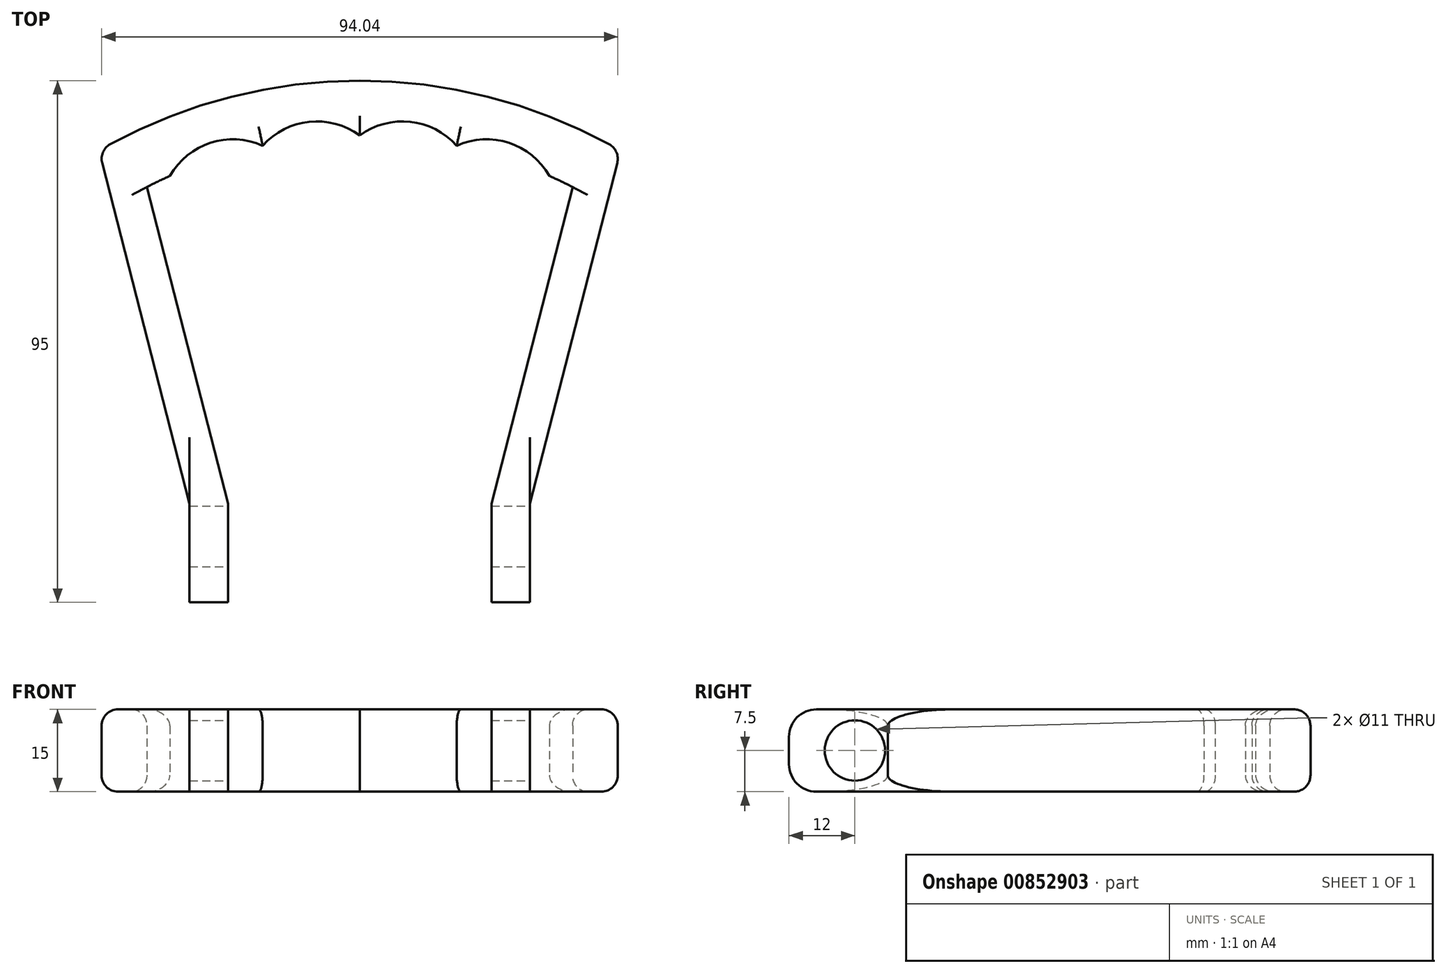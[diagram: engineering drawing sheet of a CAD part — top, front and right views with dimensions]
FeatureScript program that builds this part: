
annotation { "Feature Type Name" : "Feature", "Feature Type Description" : "" }
export const myFeature = defineFeature(function(context is Context, id is Id, definition is map)
    precondition{}
    {
        {
            var Q0;
            Q0=qCreatedBy(makeId("Top.planeOp"),FACE);
            var sketch = newSketch(context, id + "F0", { "sketchPlane" : qUnion([Q0])});
            skLineSegment(sketch, "E0.bottom", {"start": v(24, 18) * mm, "end": v(31, 18) * mm});
            skLineSegment(sketch, "E0.top", {"start": v(24, 0) * mm, "end": v(31, 0) * mm});
            skLineSegment(sketch, "E0.left", {"start": v(24, 18) * mm, "end": v(24, 0) * mm});
            skLineSegment(sketch, "E0.right", {"start": v(31, 18) * mm, "end": v(31, 0) * mm});
            skLineSegment(sketch, "E1.bottom", {"start": v(-31, 18) * mm, "end": v(-24, 18) * mm});
            skLineSegment(sketch, "E1.top", {"start": v(-31, 0) * mm, "end": v(-24, 0) * mm});
            skLineSegment(sketch, "E1.left", {"start": v(-31, 18) * mm, "end": v(-31, 0) * mm});
            skLineSegment(sketch, "E1.right", {"start": v(-24, 18) * mm, "end": v(-24, 0) * mm});
            skArc(sketch, "E2", {"start": v(-47.5, 82.27) * mm, "mid": v(0, 95) * mm, "end": v(47.5, 82.27) * mm});
            skArc(sketch, "E3", {"start": v(-42.5, 73.61) * mm, "mid": v(0, 85) * mm, "end": v(42.5, 73.61) * mm});
            skLineSegment(sketch, "E4", {"start": v(-47.5, 82.27) * mm, "end": v(0, 0) * mm, "construction": true});
            skLineSegment(sketch, "E5", {"start": v(47.5, 82.27) * mm, "end": v(0, 0) * mm, "construction": true});
            skLineSegment(sketch, "E6", {"start": v(-31, 18) * mm, "end": v(-47.5, 82.27) * mm});
            skLineSegment(sketch, "E7", {"start": v(-24, 18) * mm, "end": v(-38.8, 75.63) * mm});
            skLineSegment(sketch, "E8", {"start": v(31, 18) * mm, "end": v(47.5, 82.27) * mm});
            skLineSegment(sketch, "E9", {"start": v(24, 18) * mm, "end": v(38.8, 75.63) * mm});
            skArc(sketch, "E10", {"start": v(-44, 76.21) * mm, "mid": v(0, 88) * mm, "end": v(44, 76.21) * mm, "construction": true});
            skLineSegment(sketch, "E11", {"start": v(0, 0) * mm, "end": v(-27.2, 83.7) * mm, "construction": true});
            skLineSegment(sketch, "E12", {"start": v(0, 0) * mm, "end": v(-9.2, 87.52) * mm, "construction": true});
            skLineSegment(sketch, "E13", {"start": v(9.2, 87.52) * mm, "end": v(0, 0) * mm, "construction": true});
            skLineSegment(sketch, "E14", {"start": v(27.2, 83.7) * mm, "end": v(0, 0) * mm, "construction": true});
            skArc(sketch, "E15", {"start": v(-17.67, 83.14) * mm, "mid": v(-27.2, 83.7) * mm, "end": v(-34.57, 77.65) * mm});
            skArc(sketch, "E16", {"start": v(0, 85) * mm, "mid": v(-9.2, 87.52) * mm, "end": v(-17.67, 83.14) * mm});
            skArc(sketch, "E17", {"start": v(17.67, 83.14) * mm, "mid": v(9.2, 87.52) * mm, "end": v(0, 85) * mm});
            skArc(sketch, "E18", {"start": v(34.57, 77.65) * mm, "mid": v(27.2, 83.7) * mm, "end": v(17.67, 83.14) * mm});
            skLineSegment(sketch, "E19", {"start": v(-17.67, 83.14) * mm, "end": v(0, 0) * mm, "construction": true});
            skLineSegment(sketch, "E20", {"start": v(17.67, 83.14) * mm, "end": v(0, 0) * mm, "construction": true});
            skSolve(sketch);
        }
        {
            var Q0;
            Q0=makeQuery(id+"F0.imprint","IMPRINT",FACE,{"disambiguationData":[TD([[makeQuery(id+"F0.imprint","IMPRINT",EDGE,{"derivedFrom":sQuery(id+"F0.wireOp",EDGE,"E0.bottom")}),1.0]])]});
            var Q1;
            Q1=makeQuery(id+"F0.imprint","IMPRINT",FACE,{"disambiguationData":[TD([[makeQuery(id+"F0.imprint","IMPRINT",EDGE,{"derivedFrom":sQuery(id+"F0.wireOp",EDGE,"E1.bottom")}),-1.0]])]});
            var Q2;
            Q2=makeQuery(id+"F0.imprint","IMPRINT",FACE,{"disambiguationData":[TD([[makeQuery(id+"F0.imprint","IMPRINT",EDGE,{"derivedFrom":sQuery(id+"F0.wireOp",EDGE,"E0.bottom")}),-1.0]])]});
            extrude(context, id + "F1", {"entities" : qUnion([Q0, Q1, Q2]), "depth" : 15 * mm, "offsetDistance" : 25 * mm});
        }
        {
            var Q0;
            Q0=makeQuery(id+"F1.opExtrude","CAP_EDGE",EDGE,{"disambiguationData":[OSD([sQuery(id+"F0.wireOp",EDGE,"E9")])],"isStart":false});
            var Q1;
            {var subQ0=sQuery(id+"F0.wireOp",EDGE,"E3");Q1=makeQuery(id+"F1.opExtrude","CAP_EDGE",EDGE,{"disambiguationData":[OSD([subQ0]),TDD([makeQuery(id+"F0.imprint","IMPRINT",EDGE,{"disambiguationData":[TD([[makeQuery(id+"F0.imprint","INTERSECT",VERTEX,{"derivedFrom":[subQ0,sQuery(id+"F0.wireOp",EDGE,"E9")]}),1.0]])],"derivedFrom":subQ0})])],"isStart":false});}
            var Q2;
            Q2=makeQuery(id+"F1.opExtrude","CAP_EDGE",EDGE,{"disambiguationData":[OSD([sQuery(id+"F0.wireOp",EDGE,"E18")])],"isStart":false});
            var Q3;
            Q3=makeQuery(id+"F1.opExtrude","CAP_EDGE",EDGE,{"disambiguationData":[OSD([sQuery(id+"F0.wireOp",EDGE,"E17")])],"isStart":false});
            var Q4;
            Q4=makeQuery(id+"F1.opExtrude","CAP_EDGE",EDGE,{"disambiguationData":[OSD([sQuery(id+"F0.wireOp",EDGE,"E16")])],"isStart":false});
            var Q5;
            {var subQ0=sQuery(id+"F0.wireOp",EDGE,"E3");Q5=makeQuery(id+"F1.opExtrude","CAP_EDGE",EDGE,{"disambiguationData":[OSD([subQ0]),TDD([makeQuery(id+"F0.imprint","IMPRINT",EDGE,{"disambiguationData":[TD([[makeQuery(id+"F0.imprint","INTERSECT",VERTEX,{"derivedFrom":[subQ0,sQuery(id+"F0.wireOp",EDGE,"E7")]}),-1.0]])],"derivedFrom":subQ0})])],"isStart":false});}
            var Q6;
            Q6=makeQuery(id+"F1.opExtrude","CAP_EDGE",EDGE,{"disambiguationData":[OSD([sQuery(id+"F0.wireOp",EDGE,"E15")])],"isStart":false});
            var Q7;
            Q7=makeQuery(id+"F1.opExtrude","CAP_EDGE",EDGE,{"disambiguationData":[OSD([sQuery(id+"F0.wireOp",EDGE,"E7")])],"isStart":false});
            var Q8;
            Q8=makeQuery(id+"F1.opExtrude","CAP_EDGE",EDGE,{"disambiguationData":[OSD([sQuery(id+"F0.wireOp",EDGE,"E2")])],"isStart":false});
            var Q9;
            Q9=makeQuery(id+"F1.opExtrude","CAP_EDGE",EDGE,{"disambiguationData":[OSD([sQuery(id+"F0.wireOp",EDGE,"E6")])],"isStart":false});
            var Q10;
            Q10=makeQuery(id+"F1.opExtrude","CAP_EDGE",EDGE,{"disambiguationData":[OSD([sQuery(id+"F0.wireOp",EDGE,"E8")])],"isStart":false});
            var Q11;
            Q11=makeQuery(id+"F1.opExtrude","CAP_EDGE",EDGE,{"disambiguationData":[OSD([sQuery(id+"F0.wireOp",EDGE,"E6")])],"isStart":true});
            var Q12;
            Q12=makeQuery(id+"F1.opExtrude","CAP_EDGE",EDGE,{"disambiguationData":[OSD([sQuery(id+"F0.wireOp",EDGE,"E7")])],"isStart":true});
            var Q13;
            Q13=makeQuery(id+"F1.opExtrude","CAP_EDGE",EDGE,{"disambiguationData":[OSD([sQuery(id+"F0.wireOp",EDGE,"E9")])],"isStart":true});
            var Q14;
            Q14=makeQuery(id+"F1.opExtrude","CAP_EDGE",EDGE,{"disambiguationData":[OSD([sQuery(id+"F0.wireOp",EDGE,"E2")])],"isStart":true});
            var Q15;
            {var subQ0=sQuery(id+"F0.wireOp",EDGE,"E3");Q15=makeQuery(id+"F1.opExtrude","CAP_EDGE",EDGE,{"disambiguationData":[OSD([subQ0]),TDD([makeQuery(id+"F0.imprint","IMPRINT",EDGE,{"disambiguationData":[TD([[makeQuery(id+"F0.imprint","INTERSECT",VERTEX,{"derivedFrom":[subQ0,sQuery(id+"F0.wireOp",EDGE,"E7")]}),-1.0]])],"derivedFrom":subQ0})])],"isStart":true});}
            var Q16;
            {var subQ0=sQuery(id+"F0.wireOp",EDGE,"E3");Q16=makeQuery(id+"F1.opExtrude","CAP_EDGE",EDGE,{"disambiguationData":[OSD([subQ0]),TDD([makeQuery(id+"F0.imprint","IMPRINT",EDGE,{"disambiguationData":[TD([[makeQuery(id+"F0.imprint","INTERSECT",VERTEX,{"derivedFrom":[subQ0,sQuery(id+"F0.wireOp",EDGE,"E9")]}),1.0]])],"derivedFrom":subQ0})])],"isStart":true});}
            var Q17;
            Q17=makeQuery(id+"F1.opExtrude","CAP_EDGE",EDGE,{"disambiguationData":[OSD([sQuery(id+"F0.wireOp",EDGE,"E18")])],"isStart":true});
            var Q18;
            Q18=makeQuery(id+"F1.opExtrude","CAP_EDGE",EDGE,{"disambiguationData":[OSD([sQuery(id+"F0.wireOp",EDGE,"E17")])],"isStart":true});
            var Q19;
            Q19=makeQuery(id+"F1.opExtrude","CAP_EDGE",EDGE,{"disambiguationData":[OSD([sQuery(id+"F0.wireOp",EDGE,"E16")])],"isStart":true});
            var Q20;
            Q20=makeQuery(id+"F1.opExtrude","CAP_EDGE",EDGE,{"disambiguationData":[OSD([sQuery(id+"F0.wireOp",EDGE,"E15")])],"isStart":true});
            var Q21;
            Q21=makeQuery(id+"F1.opExtrude","CAP_EDGE",EDGE,{"disambiguationData":[OSD([sQuery(id+"F0.wireOp",EDGE,"E8")])],"isStart":true});
            var Q22;
            Q22=makeQuery(id+"F1.opExtrude","SWEPT_EDGE",EDGE,{"disambiguationData":[OSD([sQuery(id+"F0.wireOp",EDGE,"E2"),sQuery(id+"F0.wireOp",EDGE,"E6")])]});
            var Q23;
            Q23=makeQuery(id+"F1.opExtrude","SWEPT_EDGE",EDGE,{"disambiguationData":[OSD([sQuery(id+"F0.wireOp",EDGE,"E2"),sQuery(id+"F0.wireOp",EDGE,"E8")])]});
            fillet(context, id + "F2", {"entities" : qUnion([Q0, Q1, Q2, Q3, Q4, Q5, Q6, Q7, Q8, Q9, Q10, Q11, Q12, Q13, Q14, Q15, Q16, Q17, Q18, Q19, Q20, Q21, Q22, Q23]), "radius" : 3 * mm, "tangentPropagation" : true, "allowEdgeOverflow" : false});
        }
        {
            var Q0;
            Q0=makeQuery(id+"F1.opExtrude","CAP_EDGE",EDGE,{"disambiguationData":[OSD([sQuery(id+"F0.wireOp",EDGE,"E0.top")])],"isStart":true});
            var Q1;
            Q1=makeQuery(id+"F1.opExtrude","CAP_EDGE",EDGE,{"disambiguationData":[OSD([sQuery(id+"F0.wireOp",EDGE,"E0.top")])],"isStart":false});
            var Q2;
            Q2=makeQuery(id+"F1.opExtrude","CAP_EDGE",EDGE,{"disambiguationData":[OSD([sQuery(id+"F0.wireOp",EDGE,"E1.top")])],"isStart":true});
            var Q3;
            Q3=makeQuery(id+"F1.opExtrude","CAP_EDGE",EDGE,{"disambiguationData":[OSD([sQuery(id+"F0.wireOp",EDGE,"E1.top")])],"isStart":false});
            fillet(context, id + "F3", {"entities" : qUnion([Q0, Q1, Q2, Q3]), "radius" : 5 * mm, "tangentPropagation" : true, "allowEdgeOverflow" : false});
        }
        {
            var Q0;
            Q0=makeQuery(id+"F1.opExtrude","SWEPT_FACE",FACE,{"disambiguationData":[OSD([sQuery(id+"F0.wireOp",EDGE,"E0.right")])]});
            var sketch = newSketch(context, id + "F4", { "sketchPlane" : qUnion([Q0])});
            skCircle(sketch, "E21", {"center": v(12, 7.5) * mm, "radius": 5.5 * mm});
            skSolve(sketch);
        }
        {
            var Q0;
            Q0=makeQuery(id+"F4.imprint","IMPRINT",FACE,{"disambiguationData":[TD([[makeQuery(id+"F4.imprint","IMPRINT",EDGE,{"derivedFrom":sQuery(id+"F4.wireOp",EDGE,"E21")}),1.0]])]});
            extrude(context, id + "F5", {"entities" : qUnion([Q0]), "operationType" : NewBodyOperationType.REMOVE, "oppositeDirection" : true, "depth" : 67 * mm, "offsetDistance" : 25 * mm});
        }
    });
